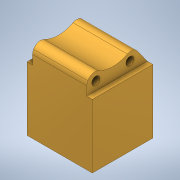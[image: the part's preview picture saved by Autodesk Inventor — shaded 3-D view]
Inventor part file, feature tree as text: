
AUTODESK INVENTOR PART (.ipt)
format: ipt  version: 2020 (Build 240168000, 168)  size: 191,488 bytes
history: native  units: in
note: dims shown in document units (in); Inventor stores cm internally (conversion verified against a paired STEP export)
features: extrude x5, sketch x5, projected_geometry x4, fillet x1
ambient origin geometry x8: Origin, YZ Plane, XZ Plane, XY Plane, X Axis, Y Axis, Z Axis, Center Point
bodies: Solid1 (feature_tree)
feature tree (15):
  extrude  "Extrusion1"  Depth=0.4523in
  extrude  "Extrusion4"  Depth=0.8586in
  extrude  "Extrusion5"  Depth=1.378in TaperAngle=0.0deg
  extrude  "Extrusion6"  Depth=0.8658in
  extrude  "Extrusion7"  Depth=1.378in TaperAngle=0.0deg
  fillet  "Fillet1"  Radius=1.5354in
  sketch  "Sketch1"  dims[d0=0.2087in d1=0.2087in d3=0.4523in]
  sketch  "Sketch4"  dims[d4=0.2118in d5=0.8586in]
  sketch  "Sketch6"  dims[d6=0.8656in d7=1.378in d8=0.0in]
  projected_geometry  "Projected Loop3"
  sketch  "Sketch7"  dims[d22=0.8658in d23=0.8658in]
  projected_geometry  "Projected Loop4"
  projected_geometry  "Projected Loop5"
  sketch  "Sketch8"  dims[d24=0.2087in d25=1.378in d26=0.0in d32=1.5354in d33=1.6535in d34=0.0in d35=1.622in d37=1.6535in d38=0.0in d39=0.7874in d40=0.3937in d41=0.0in d42=0.1969in]
  projected_geometry  "Projected Loop6"
